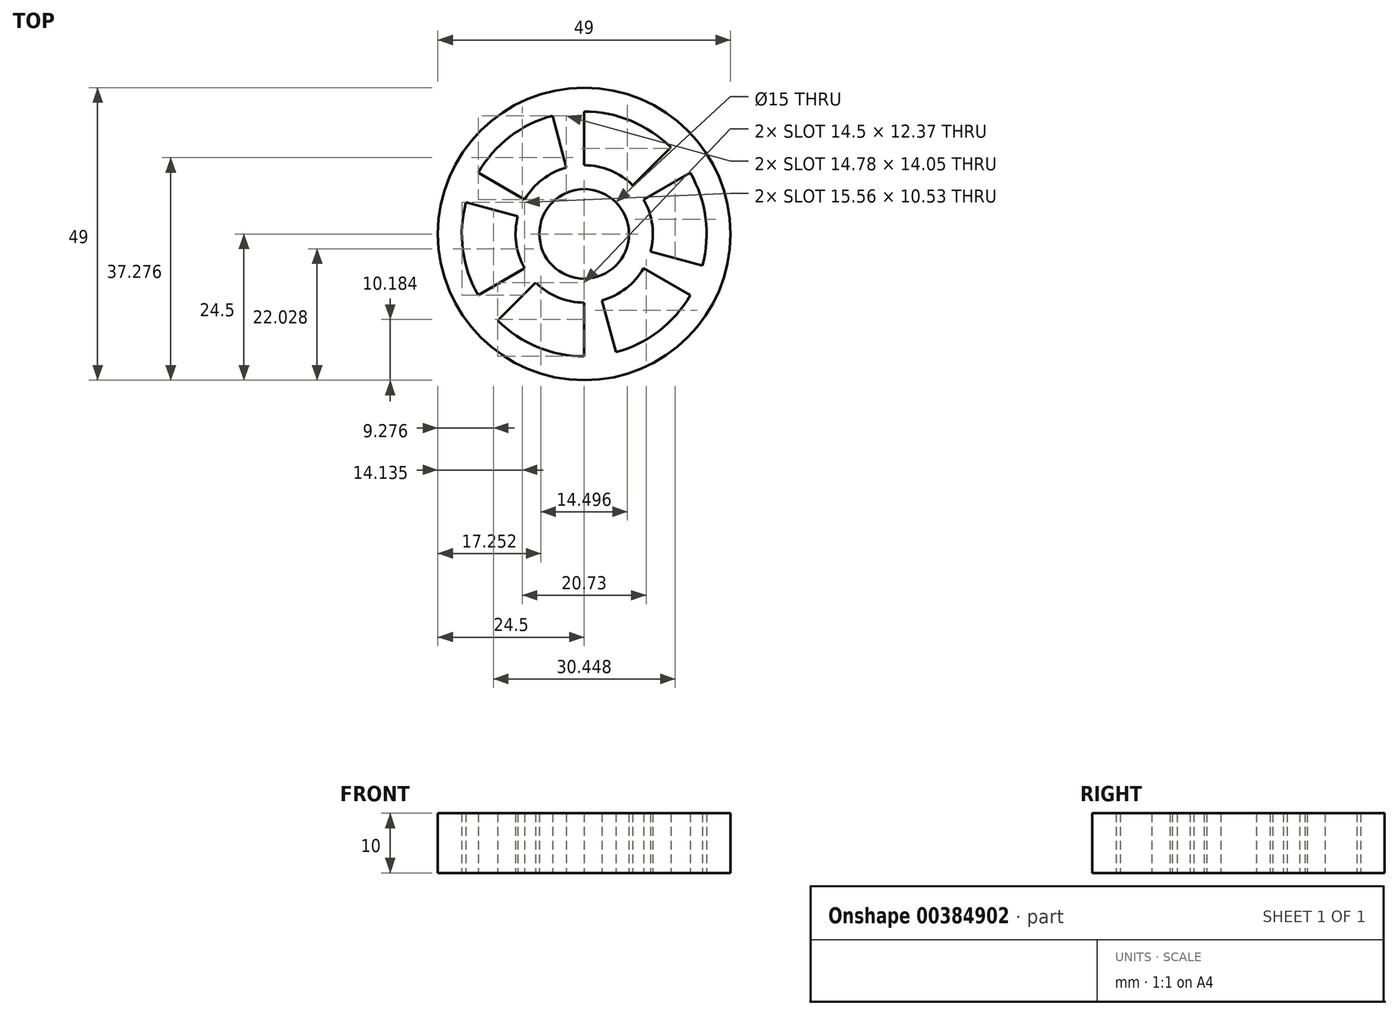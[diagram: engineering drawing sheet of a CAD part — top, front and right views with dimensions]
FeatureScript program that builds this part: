
annotation { "Feature Type Name" : "Feature", "Feature Type Description" : "" }
export const myFeature = defineFeature(function(context is Context, id is Id, definition is map)
    precondition{}
    {
        {
            var Q0;
            Q0=qCreatedBy(makeId("Top.planeOp"),FACE);
            var sketch = newSketch(context, id + "F0", { "sketchPlane" : qUnion([Q0])});
            skCircle(sketch, "E0", {"center": v(0, 0) * mm, "radius": 24.5 * mm});
            skCircle(sketch, "E1", {"center": v(0, 0) * mm, "radius": 7.5 * mm});
            skCircle(sketch, "E2", {"center": v(0, 0) * mm, "radius": 20.5 * mm, "construction": true});
            skCircle(sketch, "E3", {"center": v(0, 0) * mm, "radius": 11.5 * mm, "construction": true});
            skLineSegment(sketch, "E4", {"start": v(0, 20.5) * mm, "end": v(0, 11.5) * mm});
            skLineSegment(sketch, "E5.1.0", {"start": v(14.5, 14.5) * mm, "end": v(8.13, 8.13) * mm});
            skLineSegment(sketch, "E5.anchor1", {"start": v(0, 0) * mm, "end": v(0, 11.5) * mm, "construction": true});
            skLineSegment(sketch, "E5.anchor2", {"start": v(0, 0) * mm, "end": v(8.13, 8.13) * mm, "construction": true});
            skArc(sketch, "E6", {"start": v(0, 20.5) * mm, "mid": v(7.85, 18.94) * mm, "end": v(14.5, 14.5) * mm});
            skArc(sketch, "E7", {"start": v(0, 11.5) * mm, "mid": v(4.4, 10.62) * mm, "end": v(8.13, 8.13) * mm});
            skArc(sketch, "E8.1.0", {"start": v(17.75, 10.25) * mm, "mid": v(20.32, 2.68) * mm, "end": v(19.8, -5.3) * mm});
            skArc(sketch, "E8.1.1", {"start": v(9.96, 5.75) * mm, "mid": v(11.4, 1.5) * mm, "end": v(11.1, -2.98) * mm});
            skLineSegment(sketch, "E8.1.2", {"start": v(19.8, -5.3) * mm, "end": v(11.1, -2.98) * mm});
            skLineSegment(sketch, "E8.1.3", {"start": v(17.75, 10.25) * mm, "end": v(9.96, 5.75) * mm});
            skArc(sketch, "E8.2.0", {"start": v(17.75, -10.25) * mm, "mid": v(12.48, -16.26) * mm, "end": v(5.3, -19.8) * mm});
            skArc(sketch, "E8.2.1", {"start": v(9.96, -5.75) * mm, "mid": v(7, -9.12) * mm, "end": v(2.98, -11.1) * mm});
            skLineSegment(sketch, "E8.2.2", {"start": v(5.3, -19.8) * mm, "end": v(2.98, -11.1) * mm});
            skLineSegment(sketch, "E8.2.3", {"start": v(17.75, -10.25) * mm, "end": v(9.96, -5.75) * mm});
            skArc(sketch, "E8.3.0", {"start": v(0, -20.5) * mm, "mid": v(-7.85, -18.94) * mm, "end": v(-14.5, -14.5) * mm});
            skArc(sketch, "E8.3.1", {"start": v(0, -11.5) * mm, "mid": v(-4.4, -10.62) * mm, "end": v(-8.13, -8.13) * mm});
            skLineSegment(sketch, "E8.3.2", {"start": v(-14.5, -14.5) * mm, "end": v(-8.13, -8.13) * mm});
            skLineSegment(sketch, "E8.3.3", {"start": v(0, -20.5) * mm, "end": v(0, -11.5) * mm});
            skArc(sketch, "E8.4.0", {"start": v(-17.75, -10.25) * mm, "mid": v(-20.32, -2.68) * mm, "end": v(-19.8, 5.3) * mm});
            skArc(sketch, "E8.4.1", {"start": v(-9.96, -5.75) * mm, "mid": v(-11.4, -1.5) * mm, "end": v(-11.1, 2.98) * mm});
            skLineSegment(sketch, "E8.4.2", {"start": v(-19.8, 5.3) * mm, "end": v(-11.1, 2.98) * mm});
            skLineSegment(sketch, "E8.4.3", {"start": v(-17.75, -10.25) * mm, "end": v(-9.96, -5.75) * mm});
            skArc(sketch, "E8.5.0", {"start": v(-17.75, 10.25) * mm, "mid": v(-12.48, 16.26) * mm, "end": v(-5.3, 19.8) * mm});
            skArc(sketch, "E8.5.1", {"start": v(-9.96, 5.75) * mm, "mid": v(-7, 9.12) * mm, "end": v(-2.98, 11.1) * mm});
            skLineSegment(sketch, "E8.5.2", {"start": v(-5.3, 19.8) * mm, "end": v(-2.98, 11.1) * mm});
            skLineSegment(sketch, "E8.5.3", {"start": v(-17.75, 10.25) * mm, "end": v(-9.96, 5.75) * mm});
            skLineSegment(sketch, "E8.anchor2", {"start": v(0, 0) * mm, "end": v(-9.96, 5.75) * mm, "construction": true});
            skSolve(sketch);
        }
        {
            var Q0;
            Q0=makeQuery(id+"F0.imprint","IMPRINT",FACE,{"disambiguationData":[TD([[makeQuery(id+"F0.imprint","IMPRINT",EDGE,{"derivedFrom":sQuery(id+"F0.wireOp",EDGE,"E0")}),1.0]])]});
            extrude(context, id + "F1", {"entities" : qUnion([Q0]), "depth" : 10 * mm});
        }
    });
